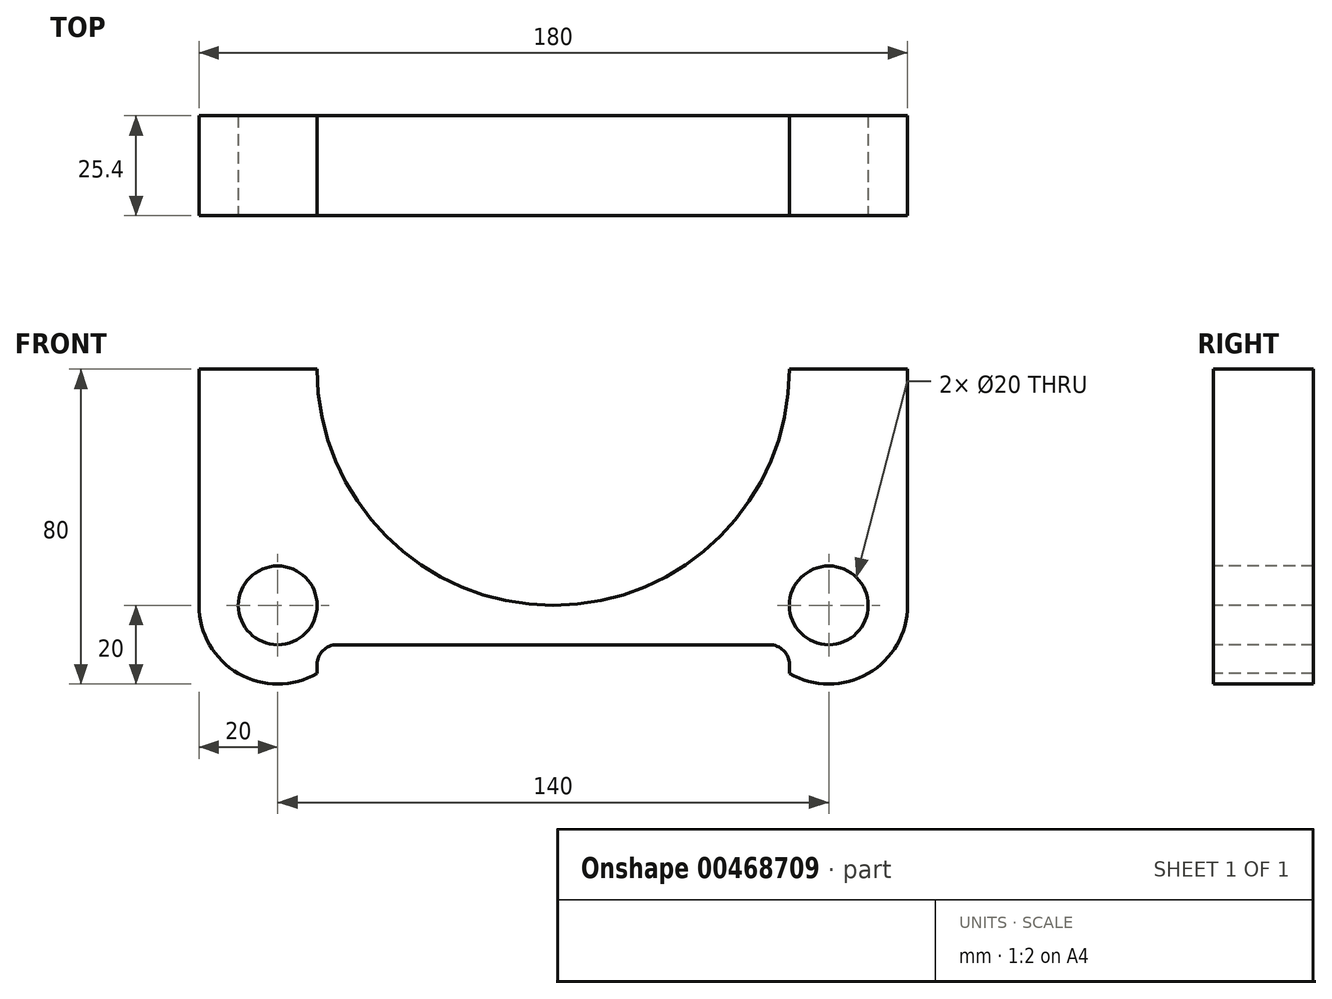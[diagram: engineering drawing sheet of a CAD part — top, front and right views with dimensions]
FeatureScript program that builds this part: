
annotation { "Feature Type Name" : "Feature", "Feature Type Description" : "" }
export const myFeature = defineFeature(function(context is Context, id is Id, definition is map)
    precondition{}
    {
        {
            var Q0;
            Q0=qCreatedBy(makeId("Front.planeOp"),FACE);
            var sketch = newSketch(context, id + "F0", { "sketchPlane" : qUnion([Q0])});
            skArc(sketch, "E0", {"start": v(-60, 0) * mm, "mid": v(0, -60) * mm, "end": v(60, 0) * mm});
            skLineSegment(sketch, "E1", {"start": v(60, 0) * mm, "end": v(90, 0) * mm});
            skLineSegment(sketch, "E2", {"start": v(90, 0) * mm, "end": v(90, -60) * mm});
            skLineSegment(sketch, "E3", {"start": v(60, -77.32) * mm, "end": v(60, -75.08) * mm});
            skLineSegment(sketch, "E4", {"start": v(54.92, -70) * mm, "end": v(0, -70) * mm});
            skLineSegment(sketch, "E5", {"start": v(70, 36.26) * mm, "end": v(70, -98.23) * mm, "construction": true});
            skPoint(sketch, "E6", {"position": v(70, -60) * mm});
            skCircle(sketch, "E7", {"center": v(70, -60) * mm, "radius": 10 * mm});
            skArc(sketch, "E8", {"start": v(60, -77.32) * mm, "mid": v(80, -77.32) * mm, "end": v(90, -60) * mm});
            skLineSegment(sketch, "E9.MirrorCS", {"start": v(-54.92, -70) * mm, "end": v(0, -70) * mm});
            skLineSegment(sketch, "E10.MirrorCS", {"start": v(-60, -77.32) * mm, "end": v(-60, -75.08) * mm});
            skArc(sketch, "E11.MirrorCS", {"start": v(-60, -77.32) * mm, "mid": v(-80, -77.32) * mm, "end": v(-90, -60) * mm});
            skLineSegment(sketch, "E12.MirrorCS", {"start": v(-90, 0) * mm, "end": v(-90, -60) * mm});
            skLineSegment(sketch, "E13.MirrorCS", {"start": v(-60, 0) * mm, "end": v(-90, 0) * mm});
            skPoint(sketch, "E14.visualSharp", {"position": v(-60, -70) * mm});
            skArc(sketch, "E14.filletArc", {"start": v(-54.92, -70) * mm, "mid": v(-58.51, -71.49) * mm, "end": v(-60, -75.08) * mm});
            skPoint(sketch, "E15.visualSharp", {"position": v(60, -70) * mm});
            skArc(sketch, "E15.filletArc", {"start": v(60, -75.08) * mm, "mid": v(58.51, -71.49) * mm, "end": v(54.92, -70) * mm});
            skCircle(sketch, "E16.MirrorC", {"center": v(-70, -60) * mm, "radius": 10 * mm});
            skLineSegment(sketch, "E17.MirrorCS", {"start": v(-70, 36.26) * mm, "end": v(-70, -98.23) * mm, "construction": true});
            skSolve(sketch);
        }
        {
            var Q0;
            Q0=makeQuery(id+"F0.imprint","IMPRINT",FACE,{"disambiguationData":[TD([[makeQuery(id+"F0.imprint","IMPRINT",EDGE,{"derivedFrom":sQuery(id+"F0.wireOp",EDGE,"E0")}),-1.0]])]});
            extrude(context, id + "F1", {"entities" : qUnion([Q0]), "endBound" : BoundingType.SYMMETRIC, "oppositeDirection" : true, "depth" : 25.4 * mm});
        }
    });
